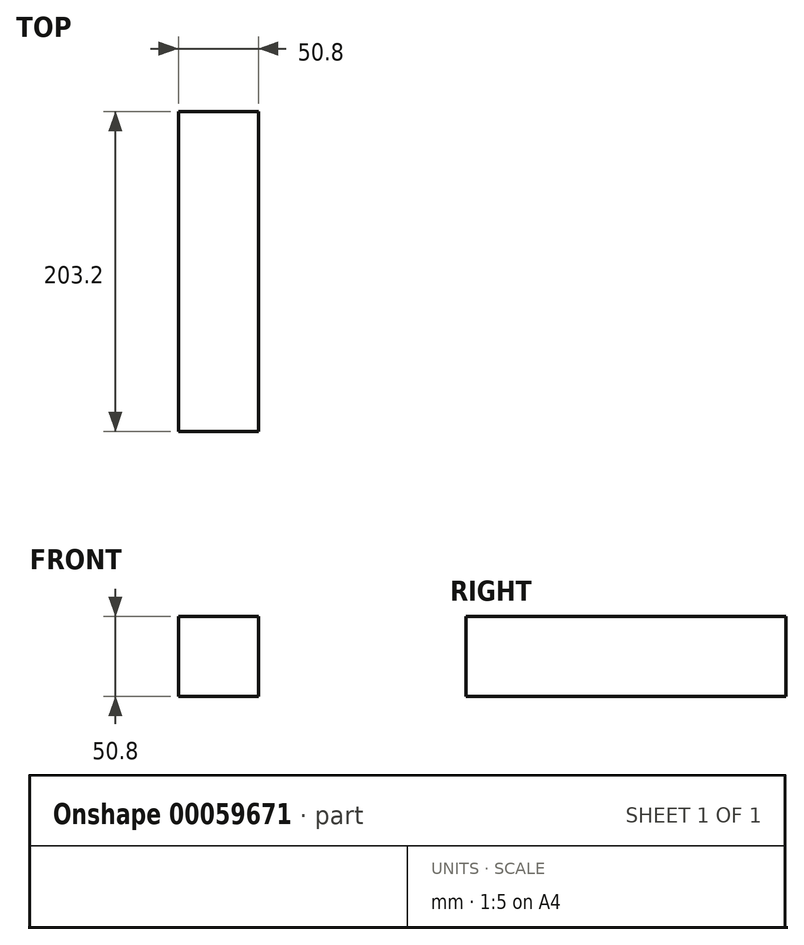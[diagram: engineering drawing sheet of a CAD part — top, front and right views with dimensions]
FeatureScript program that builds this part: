
annotation { "Feature Type Name" : "Feature", "Feature Type Description" : "" }
export const myFeature = defineFeature(function(context is Context, id is Id, definition is map)
    precondition{}
    {
        {
            var Q0;
            Q0=qCreatedBy(makeId("Front.planeOp"),FACE);
            var sketch = newSketch(context, id + "F0", { "sketchPlane" : qUnion([Q0])});
            skLineSegment(sketch, "E0.bottom", {"start": v(0, 0) * mm, "end": v(50.8, 0) * mm});
            skLineSegment(sketch, "E0.top", {"start": v(0, 50.8) * mm, "end": v(50.8, 50.8) * mm});
            skLineSegment(sketch, "E0.left", {"start": v(0, 0) * mm, "end": v(0, 50.8) * mm});
            skLineSegment(sketch, "E0.right", {"start": v(50.8, 0) * mm, "end": v(50.8, 50.8) * mm});
            skSolve(sketch);
        }
        {
            var Q0;
            Q0=makeQuery(id+"F0.imprint","IMPRINT",FACE,{"disambiguationData":[TD([[makeQuery(id+"F0.imprint","IMPRINT",EDGE,{"derivedFrom":sQuery(id+"F0.wireOp",EDGE,"E0.bottom")}),1.0]])]});
            extrude(context, id + "F1", {"entities" : qUnion([Q0]), "depth" : 203.2 * mm});
        }
    });
